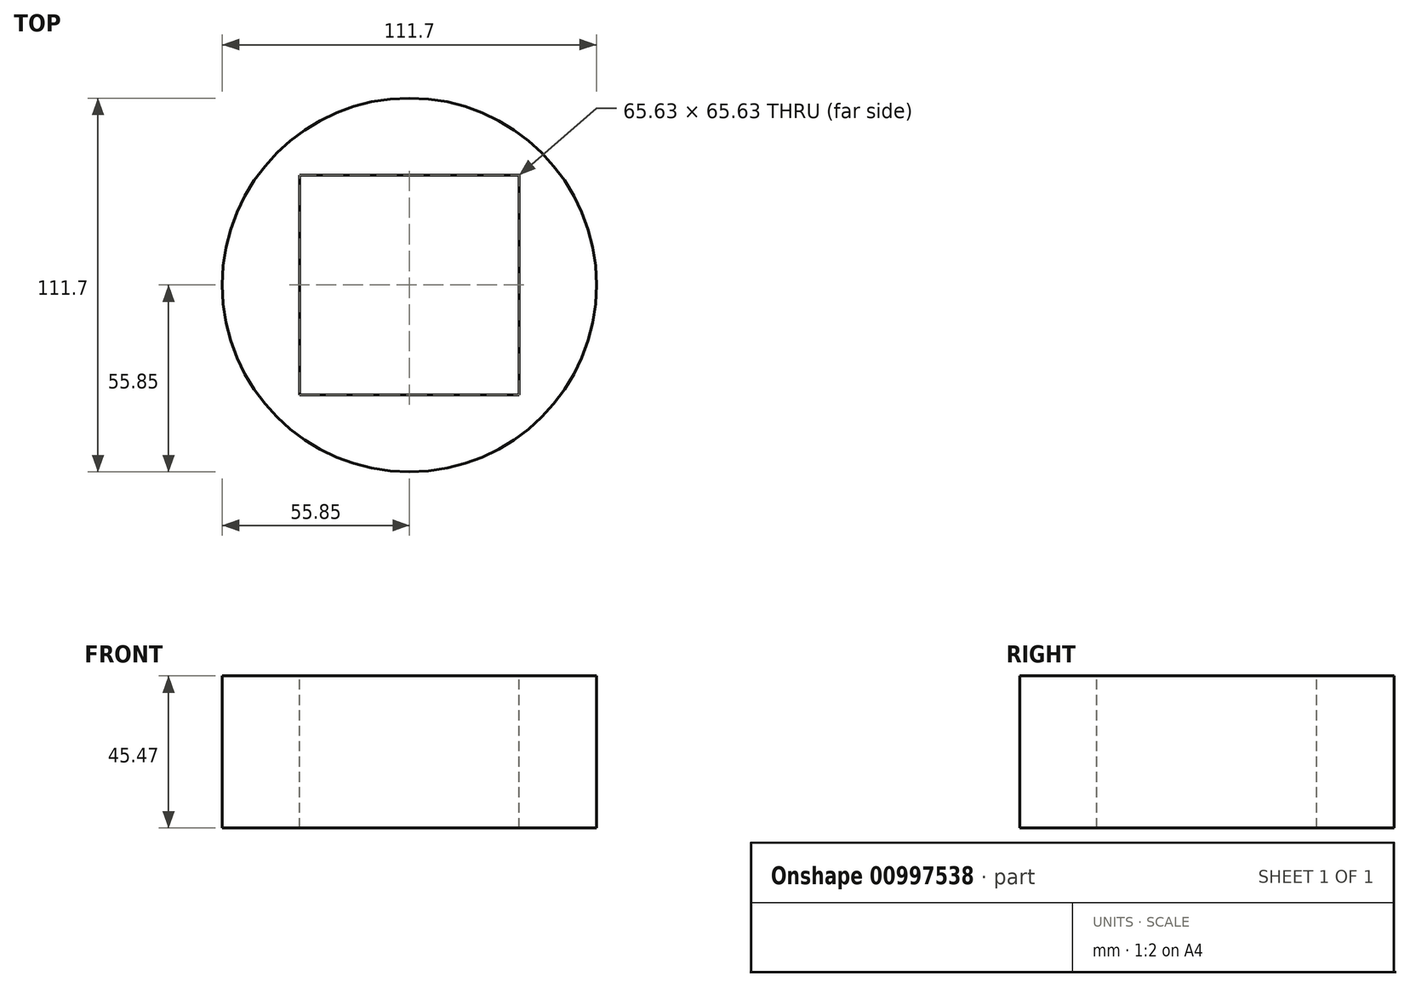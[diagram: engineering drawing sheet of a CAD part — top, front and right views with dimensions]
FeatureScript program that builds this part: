
annotation { "Feature Type Name" : "Feature", "Feature Type Description" : "" }
export const myFeature = defineFeature(function(context is Context, id is Id, definition is map)
    precondition{}
    {
        {
            var Q0;
            Q0=qCreatedBy(makeId("Top.planeOp"),FACE);
            var sketch = newSketch(context, id + "F0", { "sketchPlane" : qUnion([Q0])});
            skCircle(sketch, "E0", {"center": v(0, 0) * mm, "radius": 55.85 * mm});
            skSolve(sketch);
        }
        {
            var Q0;
            Q0=makeQuery(id+"F0.imprint","IMPRINT",FACE,{"disambiguationData":[TD([[makeQuery(id+"F0.imprint","IMPRINT",EDGE,{"derivedFrom":sQuery(id+"F0.wireOp",EDGE,"E0")}),1.0]])]});
            extrude(context, id + "F1", {"entities" : qUnion([Q0]), "depth" : 45.47 * mm, "offsetDistance" : 25.4 * mm});
        }
        {
            var Q0;
            Q0=makeQuery(id+"F1.opExtrude","CAP_FACE",FACE,{"disambiguationData":[OSD([sQuery(id+"F0.wireOp",EDGE,"E0")])],"isStart":false});
            var sketch = newSketch(context, id + "F2", { "sketchPlane" : qUnion([Q0])});
            skCircle(sketch, "E1.cCircle", {"center": v(0, 0) * mm, "radius": 32.82 * mm, "construction": true});
            skLineSegment(sketch, "E1.0", {"start": v(32.82, -32.82) * mm, "end": v(-32.82, -32.82) * mm});
            skLineSegment(sketch, "E1.1", {"start": v(-32.82, -32.82) * mm, "end": v(-32.82, 32.82) * mm});
            skLineSegment(sketch, "E1.2", {"start": v(-32.82, 32.82) * mm, "end": v(32.82, 32.82) * mm});
            skLineSegment(sketch, "E1.3", {"start": v(32.82, 32.82) * mm, "end": v(32.82, -32.82) * mm});
            skPoint(sketch, "E1.0.midPoint", {"position": v(0, -32.82) * mm});
            skSolve(sketch);
        }
        {
            var Q0;
            Q0=makeQuery(id+"F2.imprint","IMPRINT",FACE,{"disambiguationData":[TD([[makeQuery(id+"F2.imprint","IMPRINT",EDGE,{"derivedFrom":sQuery(id+"F2.wireOp",EDGE,"E1.0")}),-1.0]])]});
            extrude(context, id + "F3", {"entities" : qUnion([Q0]), "operationType" : NewBodyOperationType.REMOVE, "oppositeDirection" : true, "depth" : 64.77 * mm, "offsetDistance" : 25.4 * mm});
        }
    });
